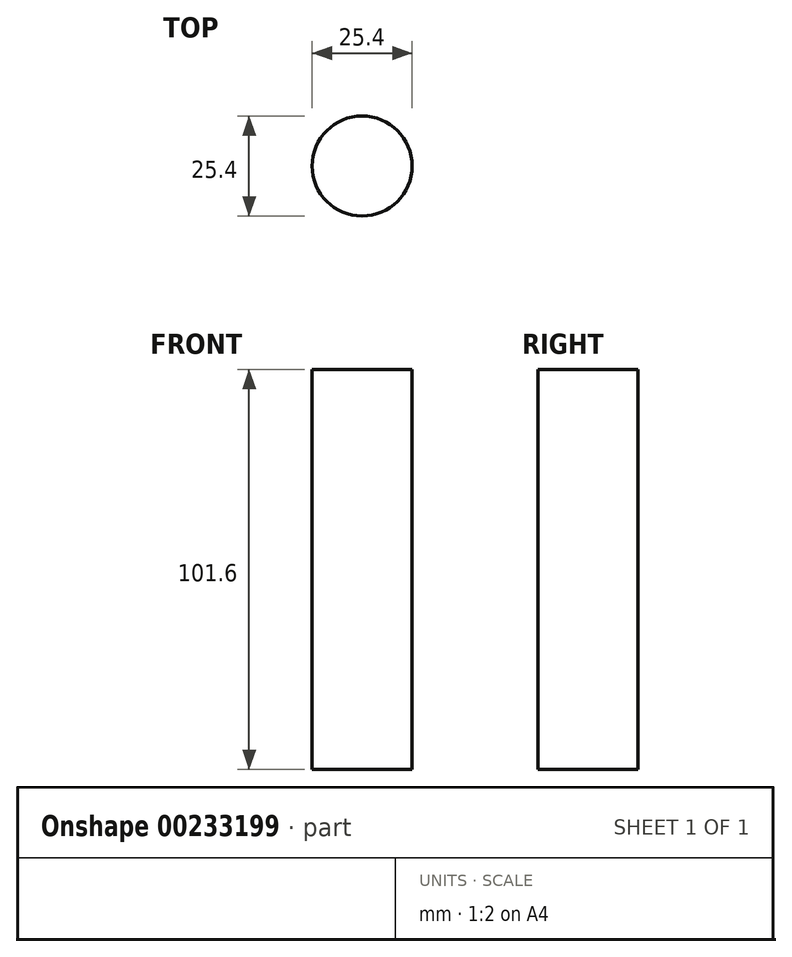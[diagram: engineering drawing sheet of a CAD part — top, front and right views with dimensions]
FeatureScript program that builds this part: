
annotation { "Feature Type Name" : "Feature", "Feature Type Description" : "" }
export const myFeature = defineFeature(function(context is Context, id is Id, definition is map)
    precondition{}
    {
        {
            var Q0;
            Q0=qCreatedBy(makeId("Top.planeOp"),FACE);
            var sketch = newSketch(context, id + "F0", { "sketchPlane" : qUnion([Q0])});
            skCircle(sketch, "E0", {"center": v(-8.28, 12.57) * mm, "radius": 12.7 * mm});
            skSolve(sketch);
        }
        {
            var Q0;
            Q0 = qSketchRegion(id + "F0", true);
            extrude(context, id + "F1", {"entities" : qUnion([Q0]), "depth" : 101.6 * mm});
        }
    });
